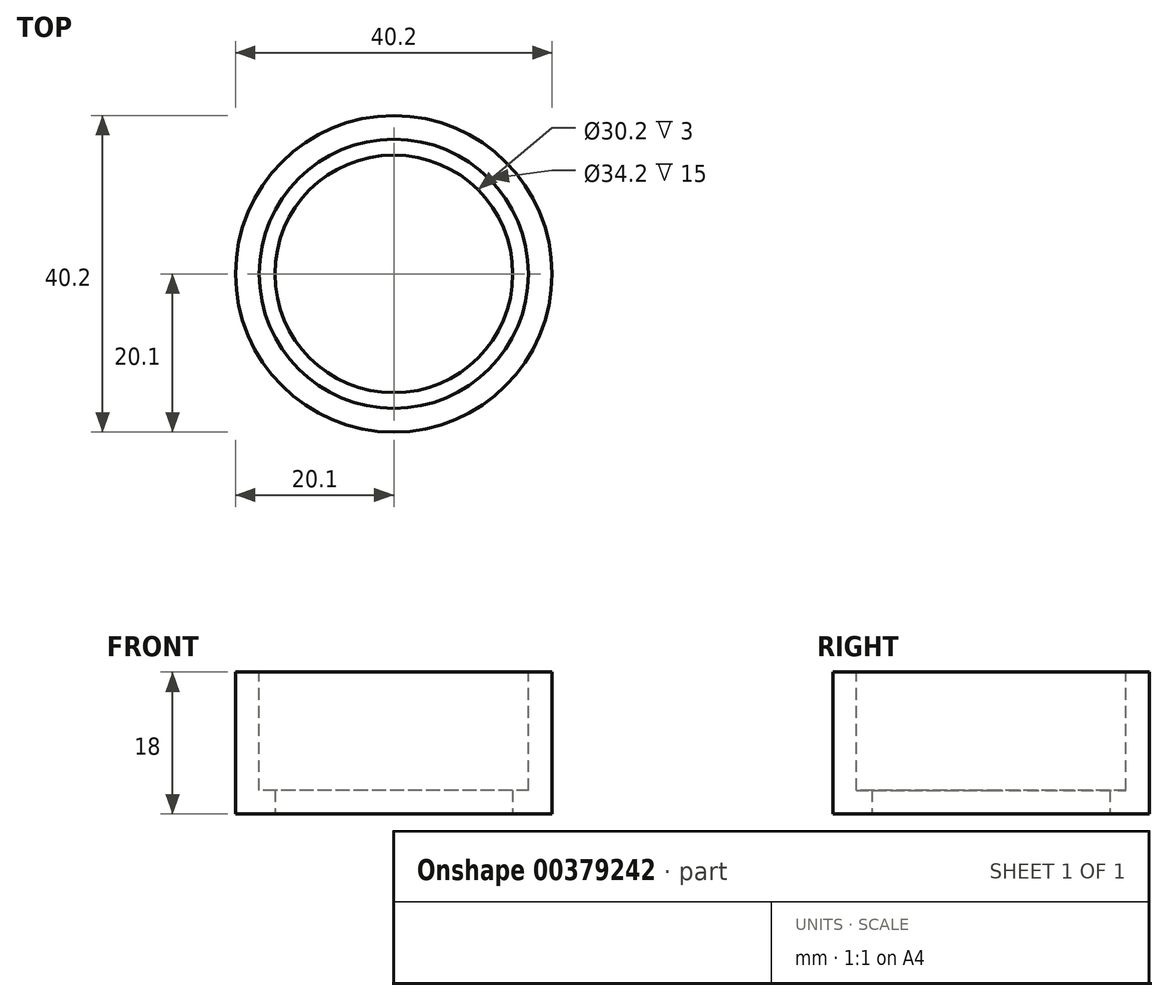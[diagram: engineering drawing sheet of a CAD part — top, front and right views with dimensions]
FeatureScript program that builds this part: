
annotation { "Feature Type Name" : "Feature", "Feature Type Description" : "" }
export const myFeature = defineFeature(function(context is Context, id is Id, definition is map)
    precondition{}
    {
        {
            assignVariable(context, id + "F0", {"name" : "h", "anyValue" : 15});
        }
        {
            var Q0;
            Q0=qCreatedBy(makeId("Top.planeOp"),FACE);
            var sketch = newSketch(context, id + "F1", { "sketchPlane" : qUnion([Q0])});
            skCircle(sketch, "E0", {"center": v(0, 0) * mm, "radius": 15.1 * mm});
            skCircle(sketch, "E1", {"center": v(0, 0) * mm, "radius": 20.1 * mm});
            skSolve(sketch);
        }
        {
            var Q0;
            Q0 = qSketchRegion(id + "F1", true);
            extrude(context, id + "F2", {"entities" : qUnion([Q0]), "depth" : (getVariable(context, 'h') + 3) * mm});
        }
        {
            var Q0;
            Q0=makeQuery(id+"F2.opExtrude","CAP_FACE",FACE,{"disambiguationData":[OSD([sQuery(id+"F1.wireOp",EDGE,"E0"),sQuery(id+"F1.wireOp",EDGE,"E1")])],"isStart":false});
            var sketch = newSketch(context, id + "F3", { "sketchPlane" : qUnion([Q0])});
            skCircle(sketch, "E2", {"center": v(0, 0) * mm, "radius": 17.1 * mm});
            skSolve(sketch);
        }
        {
            var Q0;
            Q0 = qSketchRegion(id + "F3", true);
            extrude(context, id + "F4", {"entities" : qUnion([Q0]), "operationType" : NewBodyOperationType.REMOVE, "oppositeDirection" : true, "depth" : (getVariable(context, 'h')) * mm});
        }
    });
